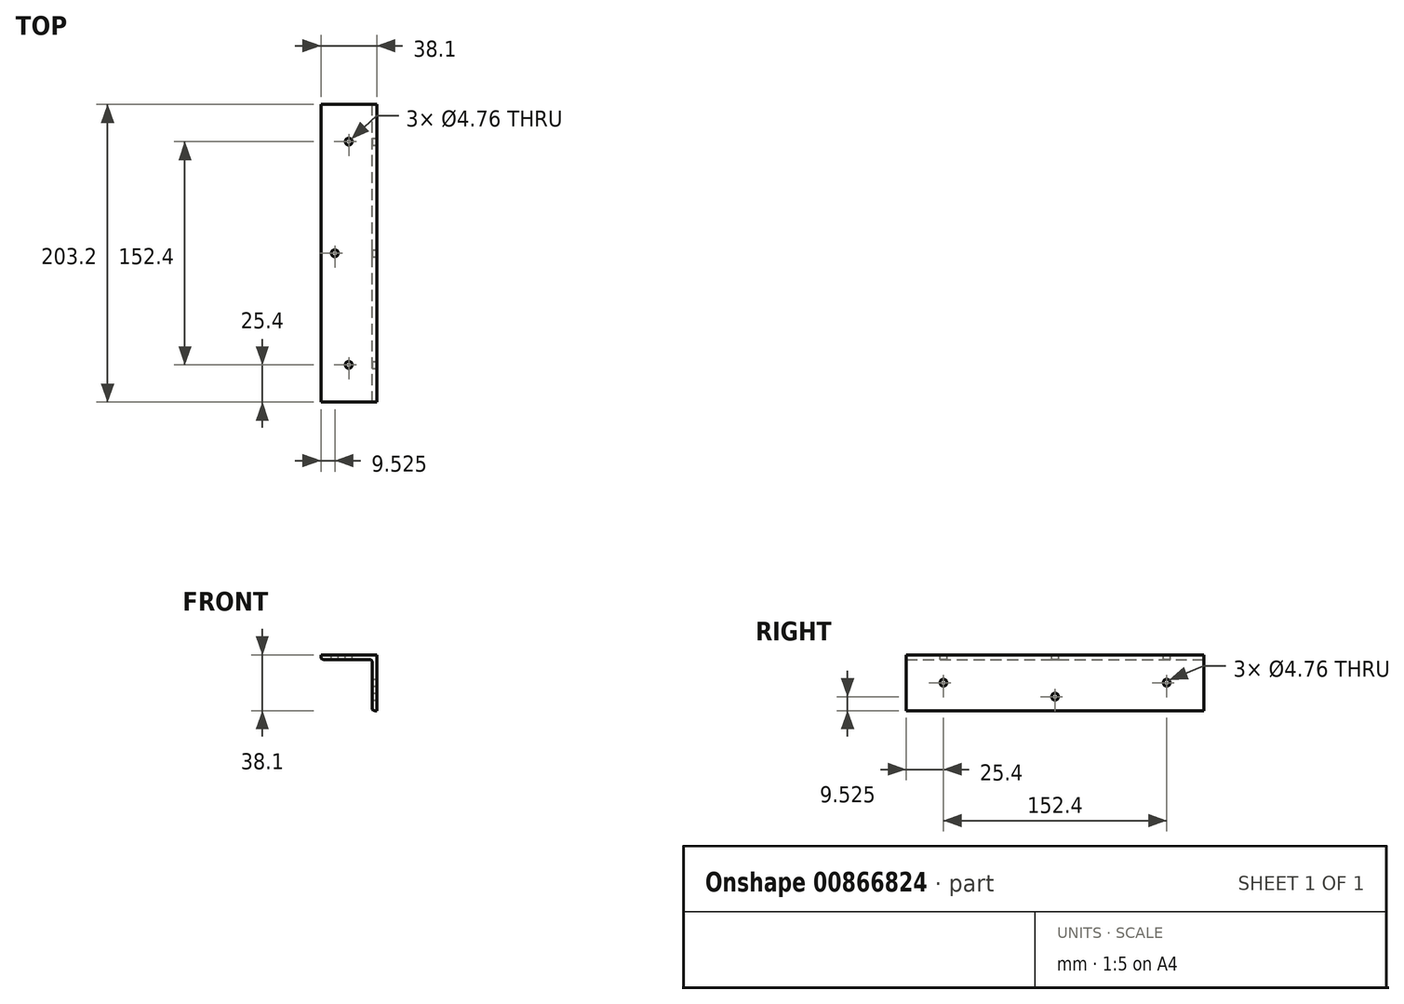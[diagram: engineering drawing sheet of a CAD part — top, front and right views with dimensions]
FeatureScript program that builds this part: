
annotation { "Feature Type Name" : "Feature", "Feature Type Description" : "" }
export const myFeature = defineFeature(function(context is Context, id is Id, definition is map)
    precondition{}
    {
        {
            var Q0;
            Q0=qCreatedBy(makeId("Front.planeOp"),FACE);
            var sketch = newSketch(context, id + "F0", { "sketchPlane" : qUnion([Q0])});
            skLineSegment(sketch, "E0", {"start": v(0, 0) * mm, "end": v(-38.1, 0) * mm});
            skLineSegment(sketch, "E1", {"start": v(-38.1, 0) * mm, "end": v(-38.1, -1.59) * mm});
            skLineSegment(sketch, "E2", {"start": v(-36.51, -3.18) * mm, "end": v(-4.76, -3.17) * mm});
            skLineSegment(sketch, "E3", {"start": v(-3.18, -4.76) * mm, "end": v(-3.17, -36.51) * mm});
            skLineSegment(sketch, "E4", {"start": v(-1.59, -38.1) * mm, "end": v(0, -38.1) * mm});
            skLineSegment(sketch, "E5", {"start": v(0, -38.1) * mm, "end": v(0, 0) * mm});
            skPoint(sketch, "E6.visualSharp", {"position": v(-38.1, -3.18) * mm});
            skArc(sketch, "E6.filletArc", {"start": v(-38.1, -1.59) * mm, "mid": v(-37.64, -2.71) * mm, "end": v(-36.51, -3.18) * mm});
            skPoint(sketch, "E7.visualSharp", {"position": v(-3.17, -38.1) * mm});
            skArc(sketch, "E7.filletArc", {"start": v(-3.17, -36.51) * mm, "mid": v(-2.71, -37.64) * mm, "end": v(-1.59, -38.1) * mm});
            skPoint(sketch, "E8.visualSharp", {"position": v(-3.18, -3.17) * mm});
            skArc(sketch, "E8.filletArc", {"start": v(-3.18, -4.76) * mm, "mid": v(-3.64, -3.64) * mm, "end": v(-4.76, -3.17) * mm});
            skSolve(sketch);
        }
        {
            var Q0;
            Q0=makeQuery(id+"F0.imprint","IMPRINT",FACE,{"disambiguationData":[TD([[makeQuery(id+"F0.imprint","IMPRINT",EDGE,{"derivedFrom":sQuery(id+"F0.wireOp",EDGE,"E0")}),1.0]])]});
            extrude(context, id + "F1", {"entities" : qUnion([Q0]), "depth" : 203.2 * mm, "offsetDistance" : 25.4 * mm});
        }
        {
            var Q0;
            Q0=makeQuery(id+"F1.opExtrude","SWEPT_FACE",FACE,{"disambiguationData":[OSD([sQuery(id+"F0.wireOp",EDGE,"E0")])]});
            var sketch = newSketch(context, id + "F2", { "sketchPlane" : qUnion([Q0])});
            skLineSegment(sketch, "E9", {"start": v(-19.05, 0) * mm, "end": v(-19.05, -203.2) * mm, "construction": true});
            skLineSegment(sketch, "E10.0", {"start": v(0, -177.8) * mm, "end": v(-38.1, -177.8) * mm, "construction": true});
            skPoint(sketch, "E11", {"position": v(-19.05, -177.8) * mm});
            skPoint(sketch, "E12", {"position": v(-19.05, -101.6) * mm});
            skLineSegment(sketch, "E13", {"start": v(-38.1, -101.6) * mm, "end": v(0, -101.6) * mm, "construction": true});
            skPoint(sketch, "E14.MirrorP", {"position": v(-19.05, -25.4) * mm});
            skPoint(sketch, "E15", {"position": v(-28.57, -101.6) * mm});
            skSolve(sketch);
        }
        {
            var Q0;
            Q0=sQuery(id+"F2.wireOp",VERTEX,"E11");
            var Q1;
            Q1=sQuery(id+"F2.wireOp",VERTEX,"E15");
            var Q2;
            Q2=sQuery(id+"F2.wireOp",VERTEX,"E14.MirrorP");
            var Q3;
            Q3=makeQuery(id+"F1.opExtrude","SWEPT_BODY",BODY,{"disambiguationData":[OSD([sQuery(id+"F0.wireOp",EDGE,"E0"),sQuery(id+"F0.wireOp",EDGE,"E1"),sQuery(id+"F0.wireOp",EDGE,"E2"),sQuery(id+"F0.wireOp",EDGE,"E3"),sQuery(id+"F0.wireOp",EDGE,"E4"),sQuery(id+"F0.wireOp",EDGE,"E5"),sQuery(id+"F0.wireOp",EDGE,"E6.filletArc"),sQuery(id+"F0.wireOp",EDGE,"E7.filletArc")])]});
            hole(context, id + "F3", {"style" : HoleStyle.SIMPLE, "endStyle" : HoleEndStyle.THROUGH, "holeDiameter" : 4.76 * mm, "majorDiameter" : 6.35 * mm, "isTappedThrough" : true, "tappedDepth" : 12.7 * mm, "tapClearance" : 3, "locations" : qUnion([Q0, Q1, Q2]), "scope" : qUnion([Q3])});
        }
        {
            var Q0;
            Q0=makeQuery(id+"F1.opExtrude","SWEPT_FACE",FACE,{"disambiguationData":[OSD([sQuery(id+"F0.wireOp",EDGE,"E5")])]});
            var sketch = newSketch(context, id + "F4", { "sketchPlane" : qUnion([Q0])});
            skLineSegment(sketch, "E16", {"start": v(-203.2, -19.05) * mm, "end": v(0, -19.05) * mm, "construction": true});
            skPoint(sketch, "E17", {"position": v(-101.6, -19.05) * mm});
            skLineSegment(sketch, "E18", {"start": v(-101.6, -38.1) * mm, "end": v(-101.6, 0) * mm, "construction": true});
            skPoint(sketch, "E19", {"position": v(-101.6, -28.57) * mm});
            skPoint(sketch, "E20", {"position": v(-25.4, -19.05) * mm});
            skPoint(sketch, "E21.MirrorP", {"position": v(-177.8, -19.05) * mm});
            skSolve(sketch);
        }
        {
            var Q0;
            Q0=sQuery(id+"F4.wireOp",VERTEX,"E20");
            var Q1;
            Q1=sQuery(id+"F4.wireOp",VERTEX,"E19");
            var Q2;
            Q2=sQuery(id+"F4.wireOp",VERTEX,"E21.MirrorP");
            var Q3;
            Q3=makeQuery(id+"F1.opExtrude","SWEPT_BODY",BODY,{"disambiguationData":[OSD([sQuery(id+"F0.wireOp",EDGE,"E0"),sQuery(id+"F0.wireOp",EDGE,"E1"),sQuery(id+"F0.wireOp",EDGE,"E2"),sQuery(id+"F0.wireOp",EDGE,"E3"),sQuery(id+"F0.wireOp",EDGE,"E4"),sQuery(id+"F0.wireOp",EDGE,"E5"),sQuery(id+"F0.wireOp",EDGE,"E6.filletArc"),sQuery(id+"F0.wireOp",EDGE,"E7.filletArc")])]});
            hole(context, id + "F5", {"style" : HoleStyle.SIMPLE, "endStyle" : HoleEndStyle.THROUGH, "holeDiameter" : 4.76 * mm, "majorDiameter" : 6.35 * mm, "isTappedThrough" : true, "tappedDepth" : 12.7 * mm, "tapClearance" : 3, "locations" : qUnion([Q0, Q1, Q2]), "scope" : qUnion([Q3])});
        }
    });
